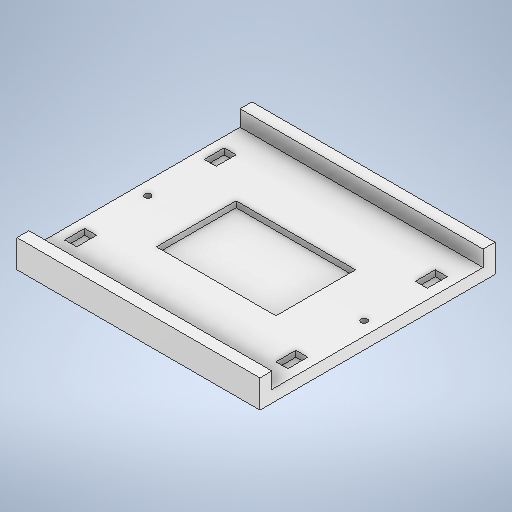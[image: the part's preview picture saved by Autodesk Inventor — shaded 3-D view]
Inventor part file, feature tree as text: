
AUTODESK INVENTOR PART (.ipt)
format: ipt  version: 2025 (Build 290162000, 162)  size: 303,104 bytes
history: native  units: in
note: dims shown in document units (in); Inventor stores cm internally (conversion verified against a paired STEP export)
features: sketch x4, extrude x3, hole x1
ambient origin geometry x8: Origin, YZ Plane, XZ Plane, XY Plane, X Axis, Y Axis, Z Axis, Center Point
bodies: Solid1 (feature_tree)
feature tree (8):
  extrude  "Extrusion1"  Depth=2.4016in
  extrude  "Extrusion2"  Depth=2.0866in
  hole  "Hole1"  [1 undecoded]
  extrude  "Extrusion4"  Depth=0.0591in
  sketch  "Sketch1"  dims[d0=2.3228in d1=2.4016in]
  sketch  "Sketch2"  dims[d2=0.2756in d3=0.0in d4=2.0866in]
  sketch  "Sketch3"  dims[d5=0.1575in d6=0.0in d7=1.0689in d8=1.0689in]
  sketch  "Sketch5"  dims[d9=0.0617in d10=0.1575in d11=0.1732in d12=0.0787in d13=90.0deg d14=2.3622in d15=0.0in d23=1.0689in d24=1.1811in d25=0.7874in d26=0.1969in d27=0.1181in d28=0.1969in d29=0.1181in d30=0.1969in d31=0.1181in d32=0.1969in d33=0.1181in d35=0.9843in d36=0.5906in d38=0.9843in d39=0.5906in d40=0.0591in d41=0.0in]
note: 1 required parameter value undecoded (feature->parameter linkage not recoverable at this tier; creation-order binding heuristic only, values carry confidence <= 0.55)
